# Revit family: SNS MERLIN GAS SOLENOID VALVE 12
name_source: partatom
category: Plumbing Fixtures
units: mm (PartAtom-declared; Revit-internal decimal feet)

## family parameters
Always vertical = Yes
Cut with Voids When Loaded = No
OmniClass Number = 23.45.00.00
OmniClass Title = Sanitary, Laundry, and Cleaning Equipment
Part Type = Normal
Room Calculation Point = No
Round Connector Dimension = Use Diameter
Shared = No
Work Plane-Based = No

## types (1)
- SNS MERLIN GAS SOLENOID VALVE 12
    Description = AGS solenoid gas valves control the flow of natural and LP (liquefied
petroleum) gases and are suitable for use on furnaces, ovens,
atmospheric burners, commercial water heaters, rooftop make-up air
units, power burners and commercial/industrial boilers. Most commonly
they are used with our range of utility controllers and gas detection
systems.
    Manufacturer = American Gas Safety LLC
    Model = AGS_Gas Solenoid Valve LV12
    Type Comments = AGS solenoid gas valves control the flow of natural and LP (liquefied
petroleum) gases and are suitable for use on furnaces, ovens,
atmospheric burners, commercial water heaters, rooftop make-up air
units, power burners and commercial/industrial boilers. Most commonly
they are used with our range of utility controllers and gas detection
systems.
    URL = https://americangassafety.com

## geometry (parser evidence)
native form markers: Sweep x28
no freeform markers — native parametric forms only
